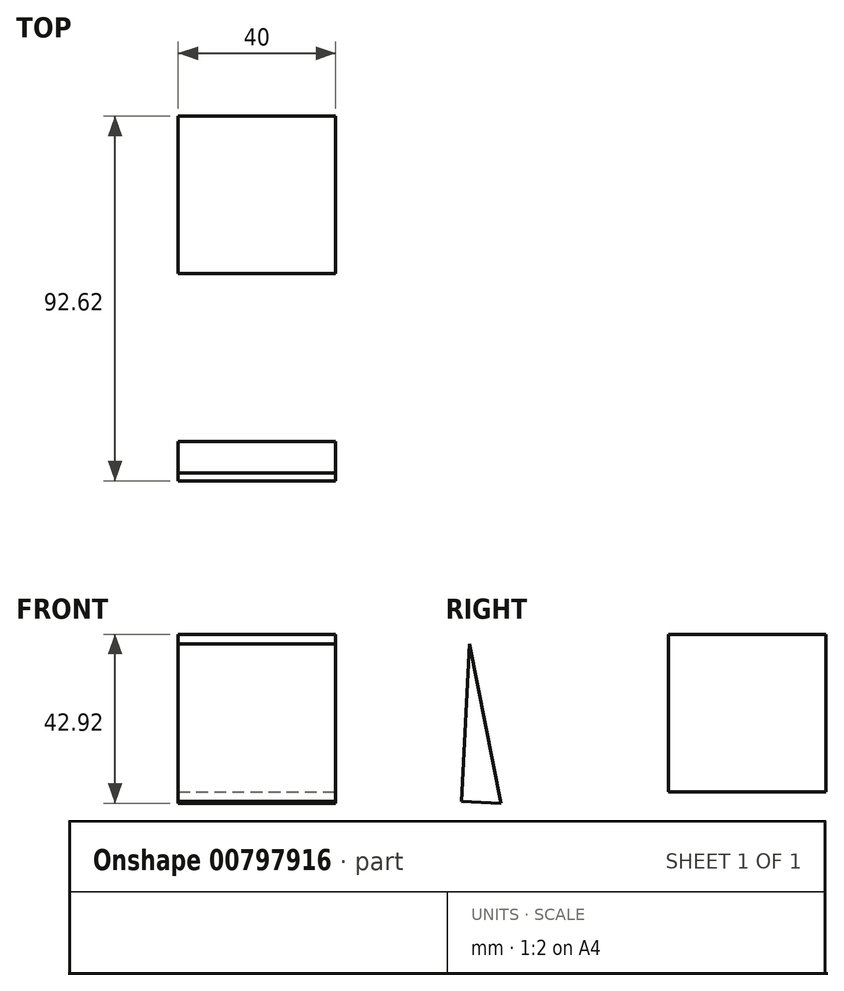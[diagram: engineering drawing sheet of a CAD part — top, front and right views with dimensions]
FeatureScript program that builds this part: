
annotation { "Feature Type Name" : "Feature", "Feature Type Description" : "" }
export const myFeature = defineFeature(function(context is Context, id is Id, definition is map)
    precondition{}
    {
        {
            var Q0;
            Q0=qCreatedBy(makeId("Top.planeOp"),FACE);
            var sketch = newSketch(context, id + "F0", { "sketchPlane" : qUnion([Q0])});
            skLineSegment(sketch, "E0", {"start": v(0, 0) * mm, "end": v(40, 0) * mm});
            skLineSegment(sketch, "E1", {"start": v(40, 0) * mm, "end": v(40, 40) * mm});
            skLineSegment(sketch, "E2", {"start": v(40, 40) * mm, "end": v(0, 40) * mm});
            skLineSegment(sketch, "E3", {"start": v(0, 40) * mm, "end": v(0, 0) * mm});
            skSolve(sketch);
        }
        {
            var Q0;
            Q0=makeQuery(id+"F0.imprint","IMPRINT",FACE,{"disambiguationData":[TD([[makeQuery(id+"F0.imprint","IMPRINT",EDGE,{"derivedFrom":sQuery(id+"F0.wireOp",EDGE,"E0")}),1.0]])]});
            extrude(context, id + "F1", {"entities" : qUnion([Q0]), "depth" : 40 * mm, "offsetDistance" : 25 * mm});
        }
        {
            var Q0;
            Q0=qCreatedBy(makeId("Right.planeOp"),FACE);
            var sketch = newSketch(context, id + "F2", { "sketchPlane" : qUnion([Q0])});
            skLineSegment(sketch, "E4", {"start": v(-50.58, 37.53) * mm, "end": v(-52.62, -2.41) * mm});
            skLineSegment(sketch, "E5", {"start": v(-52.62, -2.41) * mm, "end": v(-42.63, -2.92) * mm});
            skLineSegment(sketch, "E6", {"start": v(-42.63, -2.92) * mm, "end": v(-50.58, 37.53) * mm});
            skSolve(sketch);
        }
        {
            var Q0;
            Q0 = qSketchRegion(id + "F2", true);
            extrude(context, id + "F3", {"entities" : qUnion([Q0]), "depth" : 40 * mm, "offsetDistance" : 25 * mm});
        }
    });
